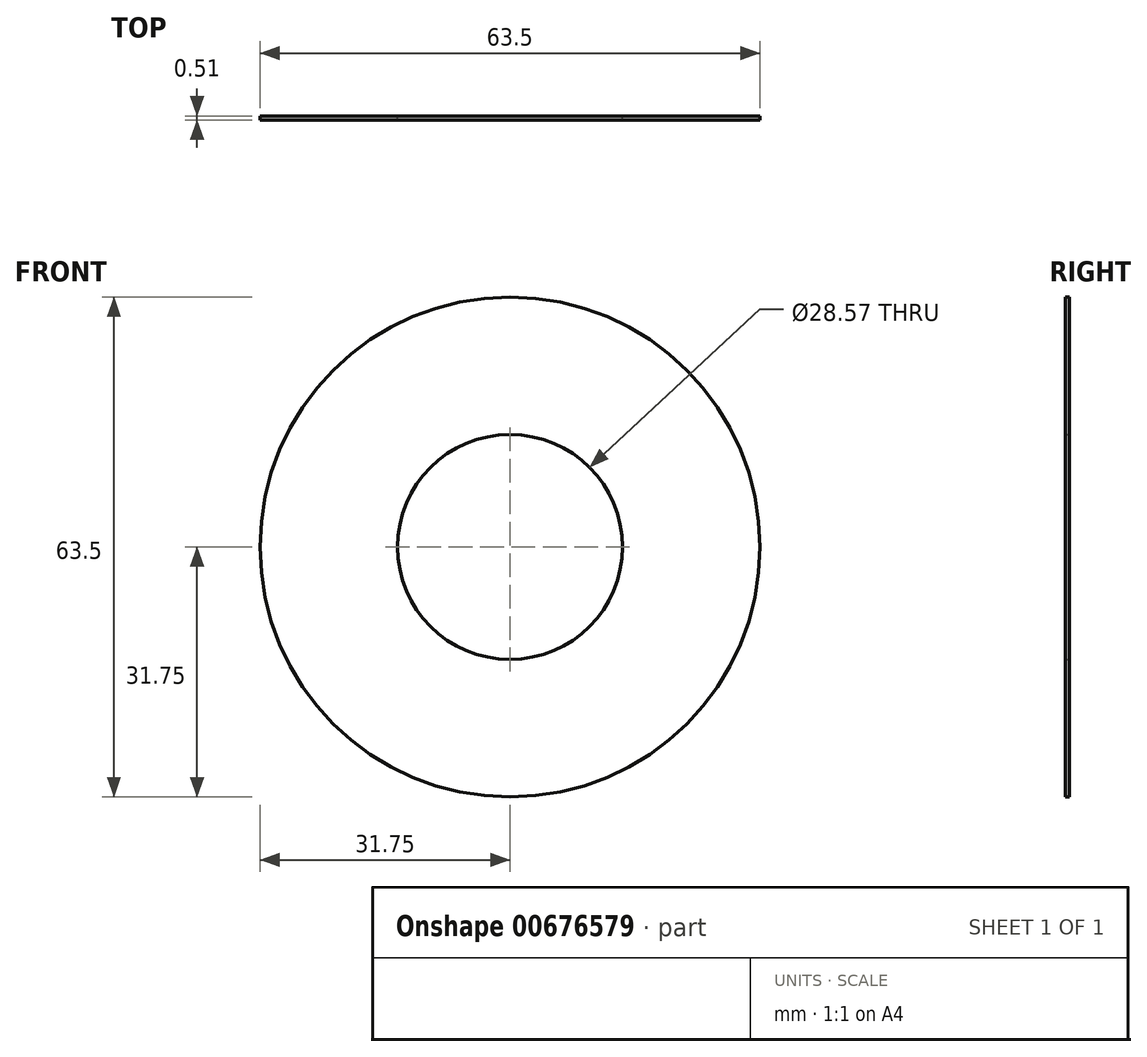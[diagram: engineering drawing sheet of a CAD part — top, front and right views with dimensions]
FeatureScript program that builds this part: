
annotation { "Feature Type Name" : "Feature", "Feature Type Description" : "" }
export const myFeature = defineFeature(function(context is Context, id is Id, definition is map)
    precondition{}
    {
        {
            var Q0;
            Q0=qCreatedBy(makeId("Front.planeOp"),FACE);
            var sketch = newSketch(context, id + "F0", { "sketchPlane" : qUnion([Q0])});
            skCircle(sketch, "E0", {"center": v(0, 0) * mm, "radius": 14.29 * mm});
            skCircle(sketch, "E1", {"center": v(0, 0) * mm, "radius": 31.75 * mm});
            skSolve(sketch);
        }
        {
            var Q0;
            Q0=makeQuery(id+"F0.imprint","IMPRINT",FACE,{"disambiguationData":[TD([[makeQuery(id+"F0.imprint","IMPRINT",EDGE,{"derivedFrom":sQuery(id+"F0.wireOp",EDGE,"E0")}),-1.0]])]});
            extrude(context, id + "F1", {"entities" : qUnion([Q0]), "depth" : 0.5 * mm, "offsetDistance" : 25.4 * mm});
        }
    });
